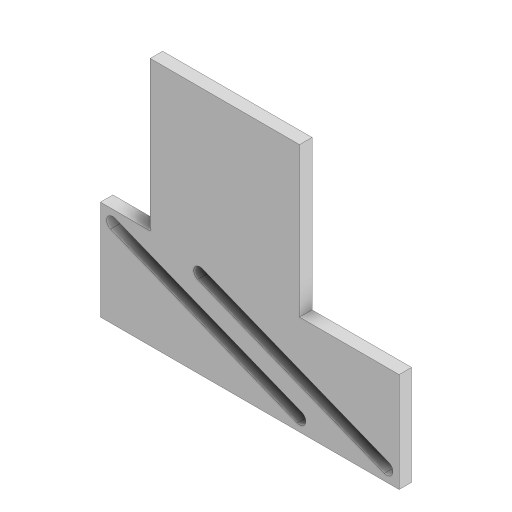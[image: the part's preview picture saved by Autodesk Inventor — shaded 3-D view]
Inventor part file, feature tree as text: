
AUTODESK INVENTOR PART (.ipt)
format: ipt  version: 2024.2 (Build 282272000, 272)  size: 120,832 bytes
history: native  units: in
note: dims shown in document units (in); Inventor stores cm internally (conversion verified against a paired STEP export)
features: extrude x1, sketch x1
ambient origin geometry x8: Origin, YZ Plane, XZ Plane, XY Plane, X Axis, Y Axis, Z Axis, Center Point
bodies: Solid1 (feature_tree)
feature tree (2):
  extrude  "Extrusion1"  Depth=0.25in TaperAngle=0.0deg
  sketch  "Sketch1"  dims[d0=3.0in d1=3.0in d2=6.0in d3=2.0in d4=1.0in d5=0.25in d6=0.25in d7=0.25in d8=0.25in d9=0.25in d10=0.25in d11=0.25in d12=0.25in d13=0.25in d14=0.0in]
